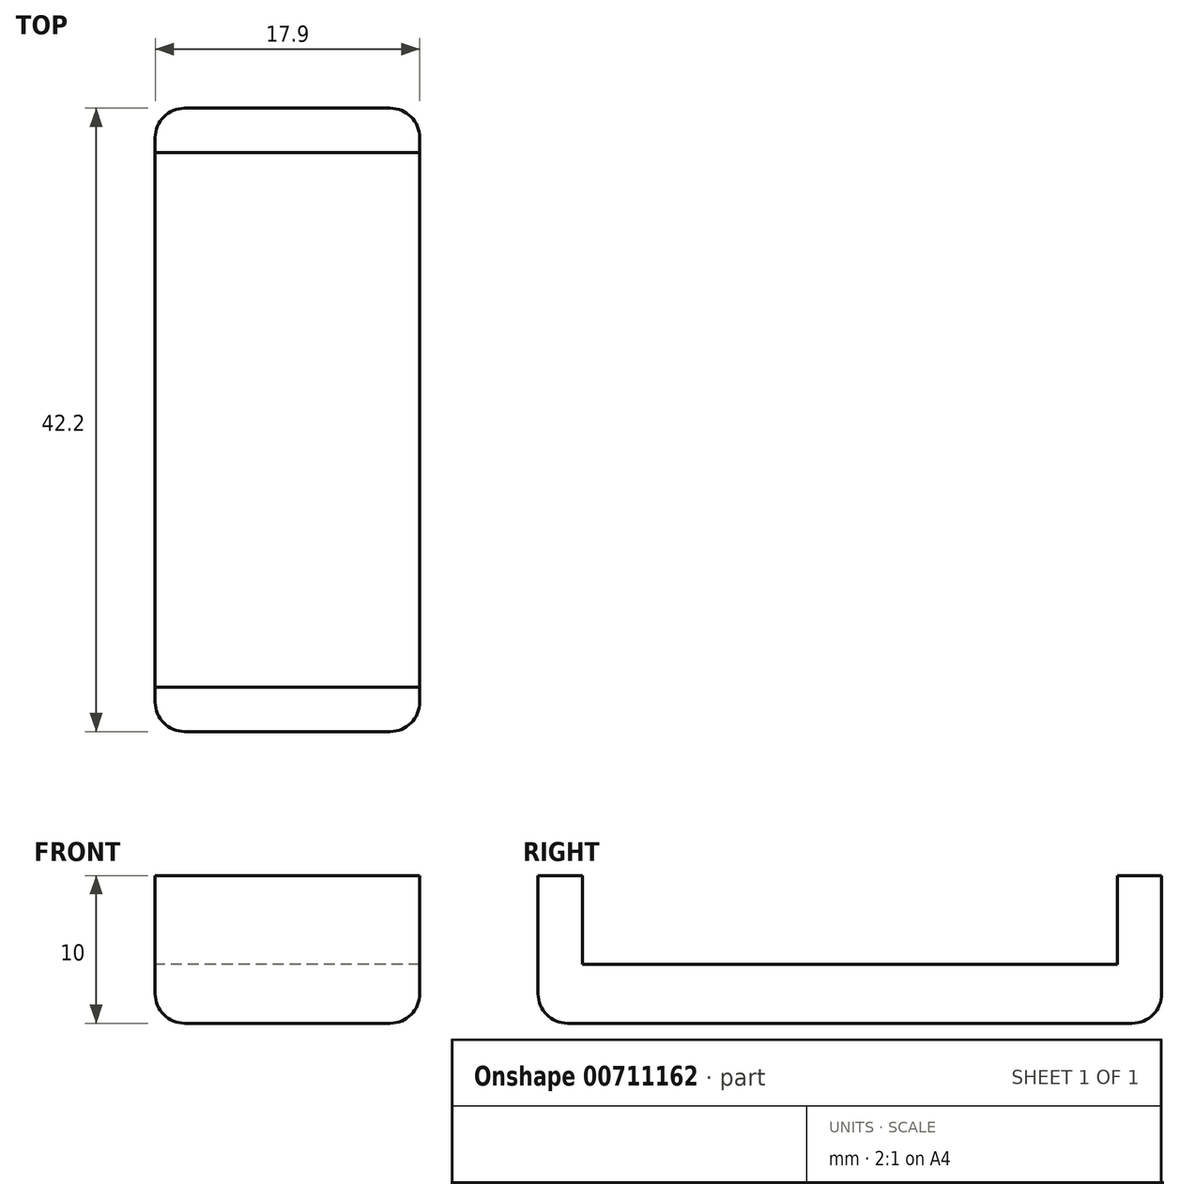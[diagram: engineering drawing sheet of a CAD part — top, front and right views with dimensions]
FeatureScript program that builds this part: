
annotation { "Feature Type Name" : "Feature", "Feature Type Description" : "" }
export const myFeature = defineFeature(function(context is Context, id is Id, definition is map)
    precondition{}
    {
        {
            var Q0;
            Q0=qCreatedBy(makeId("Top.planeOp"),FACE);
            var sketch = newSketch(context, id + "F0", { "sketchPlane" : qUnion([Q0])});
            skLineSegment(sketch, "E0.bottom", {"start": v(-23.27, 11.6) * mm, "end": v(-5.37, 11.6) * mm});
            skLineSegment(sketch, "E0.top", {"start": v(-23.27, -30.6) * mm, "end": v(-5.37, -30.6) * mm});
            skLineSegment(sketch, "E0.left", {"start": v(-23.27, 11.6) * mm, "end": v(-23.27, -30.6) * mm});
            skLineSegment(sketch, "E0.right", {"start": v(-5.37, 11.6) * mm, "end": v(-5.37, -30.6) * mm});
            skSolve(sketch);
        }
        {
            var Q0;
            Q0=makeQuery(id+"F0.imprint","IMPRINT",FACE,{"disambiguationData":[TD([[makeQuery(id+"F0.imprint","IMPRINT",EDGE,{"derivedFrom":sQuery(id+"F0.wireOp",EDGE,"E0.bottom")}),-1.0]])]});
            extrude(context, id + "F1", {"entities" : qUnion([Q0]), "depth" : 4 * mm, "offsetDistance" : 25 * mm});
        }
        {
            var Q0;
            Q0=makeQuery(id+"F1.opExtrude","CAP_FACE",FACE,{"disambiguationData":[OSD([sQuery(id+"F0.wireOp",EDGE,"E0.bottom"),sQuery(id+"F0.wireOp",EDGE,"E0.top"),sQuery(id+"F0.wireOp",EDGE,"E0.left"),sQuery(id+"F0.wireOp",EDGE,"E0.right")])],"isStart":false});
            var sketch = newSketch(context, id + "F2", { "sketchPlane" : qUnion([Q0])});
            skLineSegment(sketch, "E1.bottom", {"start": v(-5.37, 11.6) * mm, "end": v(-23.27, 11.6) * mm});
            skLineSegment(sketch, "E1.top", {"start": v(-5.37, 8.6) * mm, "end": v(-23.27, 8.6) * mm});
            skLineSegment(sketch, "E1.left", {"start": v(-5.37, 11.6) * mm, "end": v(-5.37, 8.6) * mm});
            skLineSegment(sketch, "E1.right", {"start": v(-23.27, 11.6) * mm, "end": v(-23.27, 8.6) * mm});
            skSolve(sketch);
        }
        {
            var Q0;
            Q0 = qSketchRegion(id + "F2", true);
            extrude(context, id + "F3", {"entities" : qUnion([Q0]), "operationType" : NewBodyOperationType.ADD, "depth" : 6 * mm, "offsetDistance" : 25 * mm});
        }
        {
            var Q0;
            Q0=makeQuery(id+"F1.opExtrude","CAP_FACE",FACE,{"disambiguationData":[OSD([sQuery(id+"F0.wireOp",EDGE,"E0.bottom"),sQuery(id+"F0.wireOp",EDGE,"E0.top"),sQuery(id+"F0.wireOp",EDGE,"E0.left"),sQuery(id+"F0.wireOp",EDGE,"E0.right")])],"isStart":false});
            var sketch = newSketch(context, id + "F4", { "sketchPlane" : qUnion([Q0])});
            skLineSegment(sketch, "E2.bottom", {"start": v(-5.37, -30.6) * mm, "end": v(-23.27, -30.6) * mm});
            skLineSegment(sketch, "E2.top", {"start": v(-5.37, -27.6) * mm, "end": v(-23.27, -27.6) * mm});
            skLineSegment(sketch, "E2.left", {"start": v(-5.37, -30.6) * mm, "end": v(-5.37, -27.6) * mm});
            skLineSegment(sketch, "E2.right", {"start": v(-23.27, -30.6) * mm, "end": v(-23.27, -27.6) * mm});
            skSolve(sketch);
        }
        {
            var Q0;
            Q0 = qSketchRegion(id + "F4", true);
            extrude(context, id + "F5", {"entities" : qUnion([Q0]), "operationType" : NewBodyOperationType.ADD, "depth" : 6 * mm, "offsetDistance" : 25 * mm});
        }
        {
            var Q0;
            Q0=makeQuery(id+"F1.opExtrude","CAP_EDGE",EDGE,{"disambiguationData":[OSD([sQuery(id+"F0.wireOp",EDGE,"E0.left")])],"isStart":true});
            var Q1;
            Q1=makeQuery(id+"F1.opExtrude","CAP_EDGE",EDGE,{"disambiguationData":[OSD([sQuery(id+"F0.wireOp",EDGE,"E0.right")])],"isStart":true});
            var Q2;
            Q2=makeQuery(id+"F1.opExtrude","CAP_EDGE",EDGE,{"disambiguationData":[OSD([sQuery(id+"F0.wireOp",EDGE,"E0.bottom")])],"isStart":true});
            var Q3;
            Q3=makeQuery(id+"F1.opExtrude","CAP_EDGE",EDGE,{"disambiguationData":[OSD([sQuery(id+"F0.wireOp",EDGE,"E0.top")])],"isStart":true});
            var Q4;
            Q4=makeQuery(id+"F3.boolean.opBoolean","MERGE",EDGE,{"derivedFrom":[makeQuery(id+"F1.opExtrude","SWEPT_EDGE",EDGE,{"disambiguationData":[OSD([sQuery(id+"F0.wireOp",EDGE,"E0.bottom"),sQuery(id+"F0.wireOp",EDGE,"E0.right")])]}),makeQuery(id+"F3.opExtrude","SWEPT_EDGE",EDGE,{"disambiguationData":[OSD([sQuery(id+"F2.wireOp",EDGE,"E1.bottom"),sQuery(id+"F2.wireOp",EDGE,"E1.left")])]})]});
            var Q5;
            Q5=makeQuery(id+"F3.boolean.opBoolean","MERGE",EDGE,{"derivedFrom":[makeQuery(id+"F1.opExtrude","SWEPT_EDGE",EDGE,{"disambiguationData":[OSD([sQuery(id+"F0.wireOp",EDGE,"E0.bottom"),sQuery(id+"F0.wireOp",EDGE,"E0.left")])]}),makeQuery(id+"F3.opExtrude","SWEPT_EDGE",EDGE,{"disambiguationData":[OSD([sQuery(id+"F2.wireOp",EDGE,"E1.bottom"),sQuery(id+"F2.wireOp",EDGE,"E1.right")])]})]});
            var Q6;
            Q6=makeQuery(id+"F5.boolean.opBoolean","MERGE",EDGE,{"derivedFrom":[makeQuery(id+"F1.opExtrude","SWEPT_EDGE",EDGE,{"disambiguationData":[OSD([sQuery(id+"F0.wireOp",EDGE,"E0.top"),sQuery(id+"F0.wireOp",EDGE,"E0.right")])]}),makeQuery(id+"F5.opExtrude","SWEPT_EDGE",EDGE,{"disambiguationData":[OSD([sQuery(id+"F4.wireOp",EDGE,"E2.bottom"),sQuery(id+"F4.wireOp",EDGE,"E2.left")])]})]});
            var Q7;
            Q7=makeQuery(id+"F5.boolean.opBoolean","MERGE",EDGE,{"derivedFrom":[makeQuery(id+"F1.opExtrude","SWEPT_EDGE",EDGE,{"disambiguationData":[OSD([sQuery(id+"F0.wireOp",EDGE,"E0.top"),sQuery(id+"F0.wireOp",EDGE,"E0.left")])]}),makeQuery(id+"F5.opExtrude","SWEPT_EDGE",EDGE,{"disambiguationData":[OSD([sQuery(id+"F4.wireOp",EDGE,"E2.bottom"),sQuery(id+"F4.wireOp",EDGE,"E2.right")])]})]});
            fillet(context, id + "F6", {"entities" : qUnion([Q0, Q1, Q2, Q3, Q4, Q5, Q6, Q7]), "radius" : 2 * mm, "tangentPropagation" : true, "allowEdgeOverflow" : false});
        }
    });
